# Revit family: Drinking_Fountain-Oasis-Aqua-Pointe_Sports_Bottle_Filler-M140RSBF
name_source: partatom
category: Plumbing Fixtures
revit_build: Autodesk Revit MEP 2013 (Build: 20130531_2115(x64)
units: mm (PartAtom-declared; Revit-internal decimal feet)

## types (1)
- M140RSBF
    Base Rate = 0 GPM
    CW Connection = No
    CWFU = 0
    Chiller = No
    Cold Water Connector = Cold Water Connection
    Cold Water Diameter = 0"
    Cold Water Radius = 0"
    Compression HP = 0 VA
    Default Elevation = 2' - 3"
    Description = Aqua Pointe Sports Bottle Filler
    Finish = Metal - Oasis International - Brushed Stainless Steel - Exterior Finish
    Full Load Amps = 0 A
    Manufacturer = Oasis International
    Manufacturer Fax Number = (614)322-4557
    Metal Finish = Metal - Oasis International - Brushed Stainless Steel - Exterior Finish
    Model = M140RSBF
    Product Name = Non Refrigerated, Radii Fountain w/ Integrated Sports Bottle Filler
    Rated Capacity = 0 GPM
    Rated Watts = 0 W
    Sanitary Connector = Sanitary Connection
    Sanitary Diameter = 1"
    Sanitary Radius = 1"
    URL = http://www.oasiscoolers.com
    WFU = 0
    Waste Connection = No
    Width = 3' - 2 3/4"

## geometry (parser evidence)
native form markers: Blend x8, Sweep x19
no freeform markers — native parametric forms only
